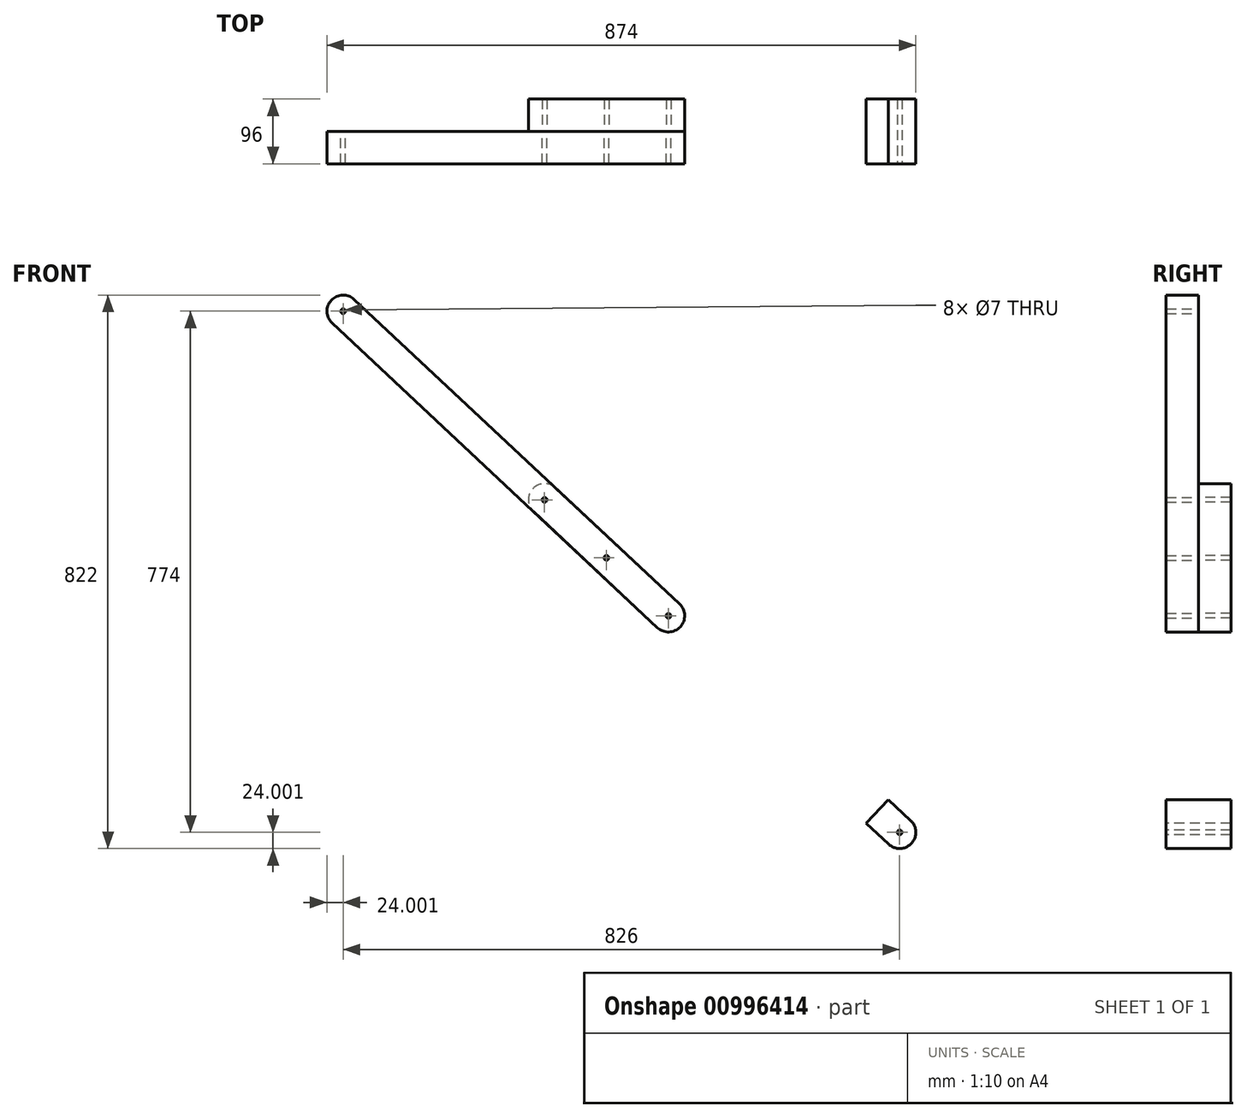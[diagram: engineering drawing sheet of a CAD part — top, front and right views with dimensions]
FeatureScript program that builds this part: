
annotation { "Feature Type Name" : "Feature", "Feature Type Description" : "" }
export const myFeature = defineFeature(function(context is Context, id is Id, definition is map)
    precondition{}
    {
        {
            var Q0;
            Q0=qCreatedBy(makeId("Front.planeOp"),FACE);
            var sketch = newSketch(context, id + "F0", { "sketchPlane" : qUnion([Q0])});
            skLineSegment(sketch, "E0", {"start": v(448.03, -425.05) * mm, "end": v(-80.71, 70.41) * mm});
            skLineSegment(sketch, "E1", {"start": v(-382.24, 287.17) * mm, "end": v(413.5, -458.47) * mm});
            skLineSegment(sketch, "E2", {"start": v(-114.64, 69.3) * mm, "end": v(-114.64, 69.3) * mm});
            skLineSegment(sketch, "E3", {"start": v(104.27, -135.82) * mm, "end": v(104.27, -135.82) * mm});
            skLineSegment(sketch, "E4", {"start": v(120.68, -118.3) * mm, "end": v(448.03, -425.05) * mm});
            skLineSegment(sketch, "E5", {"start": v(-131.05, 51.8) * mm, "end": v(87.86, -153.33) * mm});
            skLineSegment(sketch, "E6", {"start": v(413, -392.23) * mm, "end": v(380.19, -427.26) * mm});
            skLineSegment(sketch, "E7", {"start": v(413, -392.23) * mm, "end": v(448.03, -425.05) * mm});
            skCircle(sketch, "E8", {"center": v(429.91, -440.96) * mm, "radius": 3.5 * mm});
            skCircle(sketch, "E9", {"center": v(-97.13, 52.9) * mm, "radius": 3.5 * mm});
            skCircle(sketch, "E10", {"center": v(-5.18, -33.26) * mm, "radius": 3.5 * mm});
            skCircle(sketch, "E11", {"center": v(86.76, -119.4) * mm, "radius": 3.5 * mm});
            skPoint(sketch, "E12.start.orphan", {"position": v(104.27, -135.82) * mm});
            skPoint(sketch, "E13.orphan", {"position": v(-114.64, 69.3) * mm});
            skPoint(sketch, "E14.orphan", {"position": v(447.56, -457.22) * mm});
            skArc(sketch, "E15", {"start": v(413.5, -458.47) * mm, "mid": v(447.42, -457.37) * mm, "end": v(446.32, -423.45) * mm});
            skArc(sketch, "E16", {"start": v(70.35, -136.92) * mm, "mid": v(104.62, -135.44) * mm, "end": v(102.4, -101.2) * mm});
            skLineSegment(sketch, "E17", {"start": v(86.76, -119.4) * mm, "end": v(89.04, -116.76) * mm});
            skLineSegment(sketch, "E18", {"start": v(86.76, -119.4) * mm, "end": v(86.94, -122.9) * mm});
            skArc(sketch, "E19", {"start": v(-80.71, 70.41) * mm, "mid": v(-114.64, 69.3) * mm, "end": v(-113.54, 35.39) * mm});
            skLineSegment(sketch, "E20", {"start": v(-97.13, 52.9) * mm, "end": v(-94.73, 55.45) * mm});
            skLineSegment(sketch, "E21", {"start": v(-113.75, 34.88) * mm, "end": v(-113.4, 35.26) * mm});
            skLineSegment(sketch, "E22.trimOffspring", {"start": v(-99.5, 50.33) * mm, "end": v(-97.13, 52.9) * mm});
            skCircle(sketch, "E23", {"center": v(-396.09, 333.04) * mm, "radius": 3.5 * mm});
            skLineSegment(sketch, "E24", {"start": v(429.91, -440.96) * mm, "end": v(429.91, 333.04) * mm});
            skArc(sketch, "E25", {"start": v(-379.68, 350.55) * mm, "mid": v(-413.6, 349.45) * mm, "end": v(-412.5, 315.53) * mm});
            skPoint(sketch, "E26.start.orphan", {"position": v(-98.23, 86.82) * mm});
            skLineSegment(sketch, "E27", {"start": v(-379.68, 350.55) * mm, "end": v(-80.71, 70.41) * mm});
            skLineSegment(sketch, "E28", {"start": v(-382.24, 287.17) * mm, "end": v(-412.5, 315.53) * mm});
            skLineSegment(sketch, "E29", {"start": v(-396.09, 333.04) * mm, "end": v(429.91, 333.04) * mm});
            skSolve(sketch);
        }
        {
            var Q0;
            Q0=makeQuery(id+"F0.imprint","IMPRINT",FACE,{"disambiguationData":[TD([[makeQuery(id+"F0.imprint","IMPRINT",EDGE,{"derivedFrom":sQuery(id+"F0.wireOp",EDGE,"E23")}),-1.0]])]});
            var Q1;
            Q1=makeQuery(id+"F0.imprint","IMPRINT",FACE,{"disambiguationData":[TD([[makeQuery(id+"F0.imprint","IMPRINT",EDGE,{"derivedFrom":sQuery(id+"F0.wireOp",EDGE,"E10")}),-1.0]])]});
            extrude(context, id + "F1", {"entities" : qUnion([Q0, Q1]), "depth" : 48 * mm, "offsetDistance" : 25 * mm});
        }
        {
            var Q0;
            Q0=makeQuery(id+"F0.imprint","IMPRINT",FACE,{"disambiguationData":[TD([[makeQuery(id+"F0.imprint","IMPRINT",EDGE,{"derivedFrom":sQuery(id+"F0.wireOp",EDGE,"E10")}),-1.0]])]});
            var Q1;
            {var subQ5=sQuery(id+"F0.wireOp",EDGE,"E4");Q1=makeQuery(id+"F0.imprint","IMPRINT",FACE,{"disambiguationData":[TD([[makeQuery(id+"F0.imprint","IMPRINT",EDGE,{"derivedFrom":subQ5}),-1.0]])]});}
            var Q2;
            {var subQ1=sQuery(id+"F0.wireOp",EDGE,"E6");Q2=makeQuery(id+"F0.imprint","IMPRINT",FACE,{"disambiguationData":[TD([[makeQuery(id+"F0.imprint","IMPRINT",EDGE,{"derivedFrom":subQ1}),1.0]])]});}
            extrude(context, id + "F2", {"entities" : qUnion([Q0, Q1, Q2]), "oppositeDirection" : true, "depth" : 48 * mm, "offsetDistance" : 25 * mm});
        }
        {
            var Q0;
            {var subQ1=sQuery(id+"F0.wireOp",EDGE,"E6");Q0=makeQuery(id+"F0.imprint","IMPRINT",FACE,{"disambiguationData":[TD([[makeQuery(id+"F0.imprint","IMPRINT",EDGE,{"derivedFrom":subQ1}),1.0]])]});}
            extrude(context, id + "F3", {"entities" : qUnion([Q0]), "operationType" : NewBodyOperationType.ADD, "depth" : 48 * mm, "offsetDistance" : 25 * mm});
        }
    });
